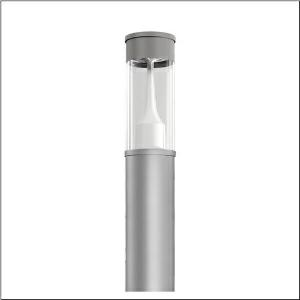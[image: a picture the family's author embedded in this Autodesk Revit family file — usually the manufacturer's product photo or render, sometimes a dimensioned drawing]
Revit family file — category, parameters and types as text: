
# Revit family: city-light_400_iq___st1_2a_5xa5305mf14hp_fa50
name_source: partatom
category: Lighting Fixtures
units: mm (PartAtom-declared; Revit-internal decimal feet)

## family parameters
Cut with Voids When Loaded = No
Host = Face
Light Source = No
Part Type = Normal
Room Calculation Point = No
Round Connector Dimension = Use Diameter
Shared = No

## types (1)
- --- (1 x LED, 4240 lm, 33.6 W, 2700K)
    Apparent Load = 34 VA
    CIE Flux Codes = 22 61 94 96 100
    Color Rendering = 70
    Color Temperature = 2700K
    Default Elevation = 1800 mm
    Description = City-Light 400 iQ, light pillar, Module 540 iQ-SR, primary light control with 3 zone facetted reflector, of plastic, silver coated, highly specular, structured, primary optical cover: cover, of PMMA, transparent, partly coated, light distribution: ST1.2a, primary light characteristic: asymmetric, LED, High Power LED, rated luminous flux: 4.240lm, luminous efficacy: 126lm/W, light colour: 727, colour temperature: 2700K, control gear: ECG iQ, control: presetting dimming logarithmic, Street-Remote, Auto-Match, Temp-Guard, Lumen-Switch, Night-Set, Smart-Wire, Light-Fading, Desk-Remote (wireless, voltage-free reading and setting of iQ features in the workshop via application-optimized NFC function/RFID function), optimised constant luminous flux control (CLO 2.0), with terminal, 6-pole, max. 2.5mm², mains connection: 230..240V, AC, 50/60Hz, start of lifetime: 34W, end of service life: 36W, reduction: 15W, luminaire housing, cylindrical, of extruded aluminium section, coated, Siteco® metallic grey (DB 702S), length: 4.694mm, diameter: 200mm, Module 540 iQ-SR, traffic white (RAL 9016), equipment: Power, protection rating (complete): IP65, insulation class (complete): insulation class II (safety insulation), certification: CE, ENEC, VDE, packaging unit: 1 piece

Light Distribution: ST1.2a
    Height = 500 mm
    Lamp = 1 x LED
    Lamp Light Flux = 4240 lm
    Lamp Power = 33.6 W
    Lamp count = 1
    Length = 200 mm  [stored 0.656168 ft]
    Luminous efficacy = 126 lm/W
    Manufacturer = Siteco
    ModVariant = No
    Model = 5XA5305MF14HP
    Mounting Place = Floor
    Mounting Type = Freestanding
    Number of Poles = 1
    OnlyDefault = Yes
    Power Factor = 1
    Product Name = City-Light 400 iQ | ST1.2a
    Product group = light pillar
    ProductGroupID = 1303
    Protection Class = Protection class II
    Protection Degree = IP 65
    RLX_Detail_Level = 1
    RLX_Emergency_Light_Flux = 0 lm
    RLX_Emergency_Type = 0
    RLX_Emergency_Type_DB = No
    RlxData = <blob elided: 53437 chars, md5=8d7fd931>
    Socket = socket
    Standby Power = 0 W
    System Light Flux = 4240 lm
    System Power = 34 W
    Type Comments = factory setting: luminous flux: 100 % | dim-lin: 254 | 695 mA
    Type Image = l_1006916.jpg
    URL = http://relux.com
    VarID = @adj_102659
    Voltage = 0 V
    Weight = 0.00 kg
    Width = 0 mm  [stored 0 ft]

note: [stored X ft] marks values corroborated as IEEE doubles in the binary element streams (Revit-internal decimal feet)

## geometry (parser evidence)
native form markers: Blend x4, Sweep x11
no freeform markers — native parametric forms only
